# Revit family: Toilet_Bariatric-Off-Floor-Whitehall-2105BAR-W-1
name_source: partatom
category: Plumbing Fixtures
units: mm (PartAtom-declared; Revit-internal decimal feet)

## family parameters
Cut with Voids When Loaded = No
Host = Face
OmniClass Number = 23.45.05.21.11.11
OmniClass Title = Water Operated Water Closets
Part Type = Normal
Room Calculation Point = No
Round Connector Dimension = Use Diameter
Shared = Yes

## types (1)
- 2105BAR-W-1
    1 - Off-Floor, Wall Outlet = Yes
    1.6 GPF = No
    3.5 GPF = No
    ADA - ADA Compliant - 18" Integral Seat Height = No
    ADA Compliant = Yes
    Assembly Code = D2010110
    BCN - Blind Cap Nuts (4) = No
    BL - Bedpan Lugs = No
    CN - Cap Nuts (4) = No
    CW Connection = Yes
    CWFU = 5
    Compliance Certifications = UPC(GREEN), WaterSense - Meets EPA Criteria certified by IAPMO R&T 1.28 gpf
    Default Elevation = 18 3/4"
    Description = Bariatric Toilet, Siphon Jet Type, Off-Floor
    EG - Enviro-Glaze: Toilet Exterior Only (Specify Color) = No
    FT - Flood-Trol (N/A for Top Supply) = No
    FTA - Flood-Trol Auto-Reset (N/A for Top Supply) = No
    FTE - Flood-Trol, Electronic = No
    FV - Flush Valve, Mechanical (N/A for ADA) = No
    FVBO - Flush Valve by Others = No
    FVH - Flush Valve, Hydraulic (N/A for Top Supply) = No
    FVL - Flush Valve, ADA Lever Handle = No
    FVT - Flush Valve Thru Wall Connector = No
    Finish = Stainless Steel-Whitehall-Satin
    HET - High Efficiency Toilet Design = No
    HET 1.28 GPF = No
    HPS - High Polish Integral Seat = No
    HSBJ - Big John Hinged Seat = No
    HW Connection = No
    HWFU = 0
    Height = 18 3/4"
    Inlet Connection Diameter = 1 1/2"
    Installation Type = Wall Mounted
    Length = 29"
    MVCFV - Time-Trol Flush Valve (N/A for Top Supply) = No
    Manufacturer = Whitehall Manufacturing
    Material = Stainless Steel-Whitehall-Satin
    Model = 2105BAR-W-1
    PFS - Punched for Seat by Others = No
    Product Documentation Link = https://www.whitehallmfg.com
    Product Page URL = https://www.whitehallmfg.com
    T - Top (Exposed) = No
    TF - Transformer, 120VAC to 24 VAC = No
    TSC - Toilet Shipping Cover = No
    URL = https://www.whitehallmfg.com
    VAC - AcornVac System = No
    Vent Connection = No
    W - Wall (Concealed) = Yes
    WFU = 5
    Waste Connection = Yes
    Waste Connection Diameter = 2 3/8"
    Width = 14"
    cUPC Compliant = Yes

## geometry (parser evidence)
native form markers: Sweep x3
no freeform markers — native parametric forms only
